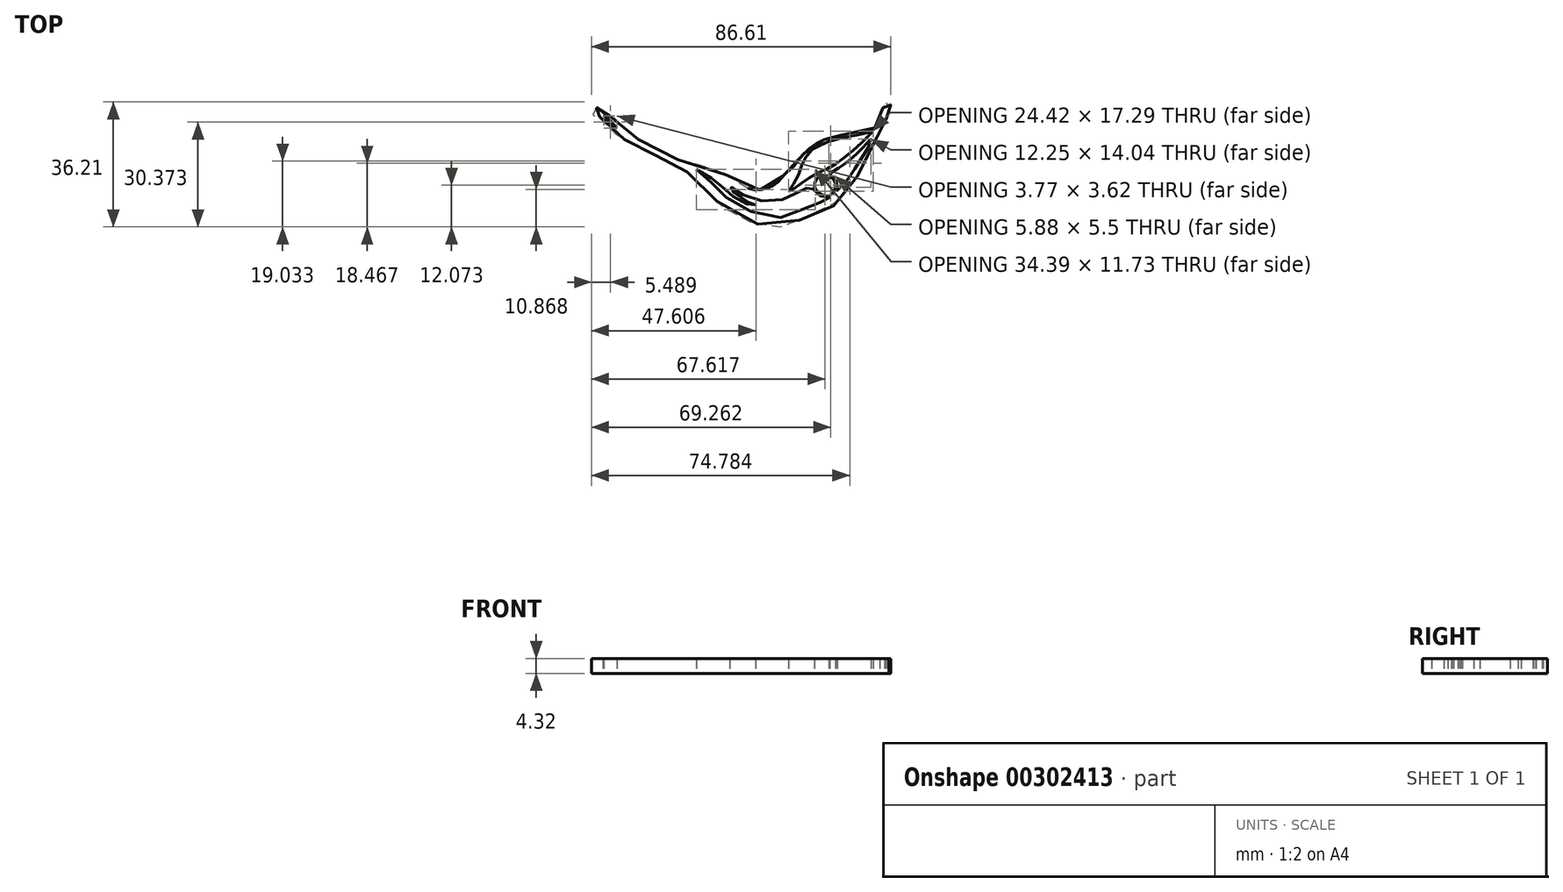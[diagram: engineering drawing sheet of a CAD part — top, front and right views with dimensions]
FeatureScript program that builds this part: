
annotation { "Feature Type Name" : "Feature", "Feature Type Description" : "" }
export const myFeature = defineFeature(function(context is Context, id is Id, definition is map)
    precondition{}
    {
        {
            var Q0;
            Q0=qCreatedBy(makeId("Top.planeOp"),FACE);
            var sketch = newSketch(context, id + "F0", { "sketchPlane" : qUnion([Q0])});
            skFitSpline(sketch, "E0", {"points": [v(-43.46, 14.38) * mm, v(-44.23, 13.82) * mm, v(-44.8, 13.18) * mm, v(-44.82, 12.68) * mm, v(-44.36, 12.07) * mm, v(-43.25, 11.92) * mm, v(-42.68, 11.9) * mm, v(-42.57, 11.9) * mm, v(-42.53, 11.75) * mm, v(-41.7, 10.3) * mm, v(-39.3, 7.87) * mm, v(-34.59, 4.74) * mm, v(-31.85, 3.4) * mm, v(-30.37, 2.4) * mm, v(-26.53, 0.67) * mm, v(-23.64, -0.81) * mm, v(-20.37, -2.4) * mm, v(-17.35, -4.13) * mm, v(-13.45, -7.38) * mm, v(-9.8, -11.5) * mm, v(-7.92, -13.38) * mm, v(-5.1, -15.68) * mm, v(2.66, -19.24) * mm, v(8.89, -20.2) * mm, v(13.19, -19.5) * mm, v(16.5, -17.42) * mm, v(19.24, -15.76) * mm, v(23.96, -14.69) * mm, v(26.11, -13.28) * mm, v(28.6, -10.38) * mm, v(30.9, -7.42) * mm, v(33.51, -2.7) * mm, v(36.14, 2.38) * mm, v(38, 6.37) * mm, v(38.5, 7.84) * mm, v(39, 8.38) * mm, v(39.55, 9.56) * mm, v(40.04, 10.09) * mm, v(40.35, 11.03) * mm, v(41.15, 11.69) * mm, v(41.15, 11.97) * mm, v(40.9, 12.98) * mm, v(40.84, 13.54) * mm, v(40.94, 13.74) * mm, v(41.47, 14.13) * mm, v(41.74, 14.96) * mm, v(41.54, 15.76) * mm, v(40.73, 16) * mm, v(40.18, 15.73) * mm, v(40, 15.17) * mm, v(40.25, 14.82) * mm, v(40.39, 14.68) * mm, v(39.83, 14.68) * mm, v(39.2, 13.81) * mm, v(38.64, 12.7) * mm, v(38.57, 11.58) * mm, v(37.8, 10.12) * mm, v(37.42, 9.29) * mm, v(37.15, 8.48) * mm, v(36.8, 8.2) * mm, v(36.24, 8) * mm, v(32.93, 7.44) * mm, v(26.45, 6.18) * mm, v(22.34, 5) * mm, v(18.2, 2.44) * mm, v(15.35, -0.53) * mm, v(13.74, -2.57) * mm, v(11.52, -4.5) * mm, v(10.67, -5.35) * mm, v(9.53, -6.82) * mm, v(7.86, -8.1) * mm, v(6.39, -8.84) * mm, v(3.57, -9.5) * mm, v(0.75, -9.15) * mm, v(-3.47, -6.61) * mm, v(-7.61, -4.31) * mm, v(-16.63, -1.54) * mm, v(-19.79, -0.7) * mm, v(-23.14, 0.88) * mm, v(-29.1, 3.83) * mm, v(-33.31, 6.66) * mm, v(-37.33, 10.5) * mm, v(-38.62, 11.54) * mm, v(-40.4, 12.37) * mm, v(-41.2, 12.78) * mm, v(-41.53, 12.66) * mm, v(-41.53, 12.96) * mm, v(-41.76, 13.84) * mm, v(-42.64, 14.43) * mm, v(-43.46, 14.38) * mm]});
            skFitSpline(sketch, "E1", {"points": [v(-14.45, -3.47) * mm, v(-11.98, -5.47) * mm, v(-8.6, -9.16) * mm, v(-4.78, -12.4) * mm, v(3.52, -16.48) * mm, v(11.92, -17.15) * mm, v(16.23, -15.05) * mm, v(20, -13.5) * mm, v(22.54, -12.67) * mm, v(23.7, -11.87) * mm, v(24.06, -11.6) * mm, v(23.7, -11.71) * mm, v(23.36, -11.76) * mm, v(22.28, -11.66) * mm, v(20.73, -10.86) * mm, v(19.84, -10.07) * mm, v(19.35, -9.27) * mm, v(19.1, -9.24) * mm, v(18.81, -9.13) * mm, v(18.34, -8.96) * mm, v(17.72, -8.93) * mm, v(16.78, -9.06) * mm, v(15.52, -9.94) * mm, v(13.74, -10.75) * mm, v(12.14, -11.6) * mm, v(9.16, -12.63) * mm, v(4.7, -12.7) * mm, v(0.45, -11.54) * mm, v(-2.41, -10.03) * mm, v(-4.02, -9.05) * mm, v(-4.68, -8.62) * mm, v(-4.8, -8.64) * mm, v(-4.78, -8.75) * mm, v(-4.2, -9.48) * mm, v(-3.27, -10.53) * mm, v(-0.57, -12.48) * mm, v(1.68, -13.47) * mm, v(2.44, -13.62) * mm, v(2.56, -13.66) * mm, v(2.63, -13.74) * mm, v(2.54, -13.8) * mm, v(2.23, -13.85) * mm, v(1.72, -13.87) * mm, v(0.62, -13.77) * mm, v(-0.47, -13.35) * mm, v(-2.89, -12.12) * mm, v(-5.08, -10.42) * mm, v(-6.62, -9.1) * mm, v(-7.7, -7.93) * mm, v(-9.64, -6.52) * mm, v(-11.55, -5.11) * mm, v(-14.45, -3.47) * mm]});
            skFitSpline(sketch, "E2", {"points": [v(12.2, -9.81) * mm, v(14.18, -7) * mm, v(15.74, -3.08) * mm, v(17.1, 0) * mm, v(19.55, 2.56) * mm, v(22.34, 4.02) * mm, v(30.1, 6.1) * mm, v(35.1, 7.05) * mm, v(36.11, 7.31) * mm, v(36.51, 7.45) * mm, v(36.62, 7.48) * mm, v(36.54, 7.38) * mm, v(35.62, 6.44) * mm, v(34.13, 5) * mm, v(30.47, 1.6) * mm, v(26.26, -1.68) * mm, v(23.17, -3.45) * mm, v(19.85, -4.99) * mm, v(15.96, -7.51) * mm, v(13.72, -9.06) * mm, v(12.2, -9.81) * mm]});
            skFitSpline(sketch, "E3", {"points": [v(23.8, -4.96) * mm, v(24.13, -5.1) * mm, v(25.71, -6.5) * mm, v(26.28, -8.03) * mm, v(26.22, -9.26) * mm, v(25.98, -9.9) * mm, v(26.37, -9.55) * mm, v(28.15, -7.77) * mm, v(29.91, -5.54) * mm, v(32.05, -2.29) * mm, v(34.42, 1.4) * mm, v(35.71, 3.98) * mm, v(36.04, 5.01) * mm, v(36.07, 5.2) * mm, v(36.07, 5.3) * mm, v(35.97, 5.22) * mm, v(35.8, 5.01) * mm, v(34.73, 3.9) * mm, v(32.75, 1.82) * mm, v(28.99, -1.45) * mm, v(27.07, -2.89) * mm, v(24.53, -4.52) * mm, v(23.8, -4.96) * mm]});
            skFitSpline(sketch, "E4", {"points": [v(23.56, -5.38) * mm, v(24.75, -5.97) * mm, v(25.7, -7.5) * mm, v(25.71, -8.83) * mm, v(25.2, -10.15) * mm, v(23.8, -11.15) * mm, v(21.76, -10.81) * mm, v(20.69, -10.11) * mm, v(19.78, -8.74) * mm, v(19.86, -7.13) * mm, v(21.02, -5.68) * mm, v(22.4, -5.25) * mm, v(23.56, -5.38) * mm]});
            skFitSpline(sketch, "E5", {"points": [v(-37.48, 8.36) * mm, v(-38.4, 9) * mm, v(-39.47, 9.7) * mm, v(-40.17, 10.38) * mm, v(-40.78, 11.08) * mm, v(-41.2, 11.88) * mm, v(-41.26, 11.99) * mm, v(-41.14, 11.94) * mm, v(-40.59, 11.5) * mm, v(-39.83, 10.94) * mm, v(-38.98, 10.06) * mm, v(-37.87, 8.86) * mm, v(-37.48, 8.36) * mm]});
            skSolve(sketch);
        }
        {
            var Q0;
            Q0 = qSketchRegion(id + "F0", true);
            extrude(context, id + "F1", {"entities" : qUnion([Q0]), "depth" : 4.32 * mm});
        }
    });
